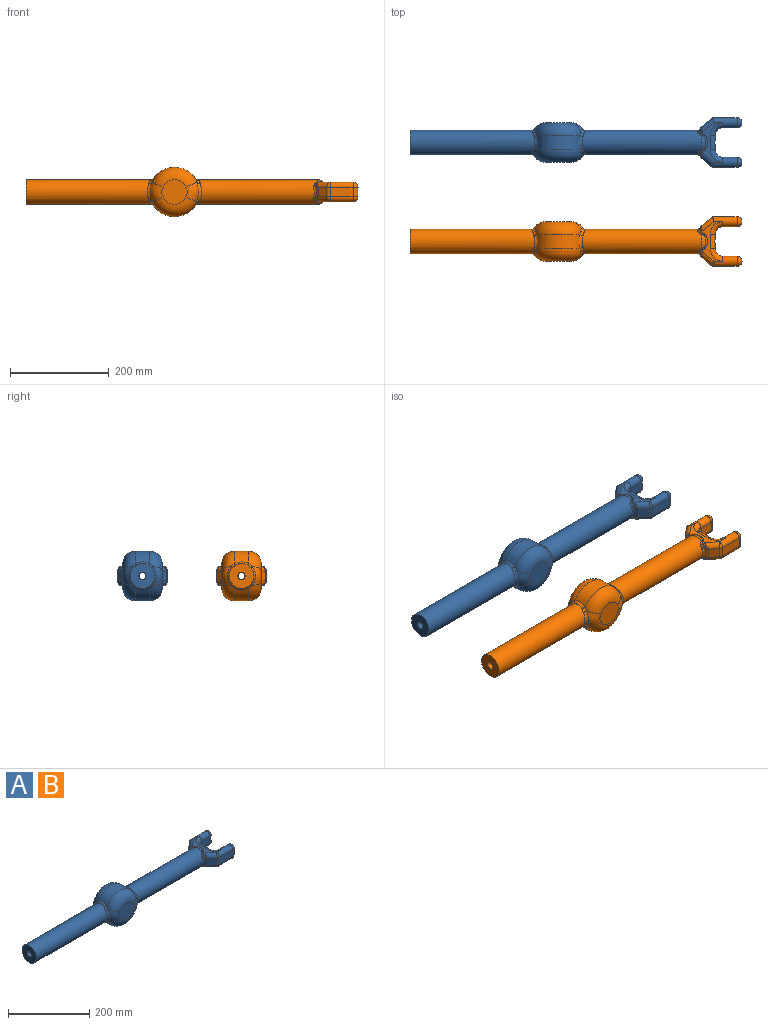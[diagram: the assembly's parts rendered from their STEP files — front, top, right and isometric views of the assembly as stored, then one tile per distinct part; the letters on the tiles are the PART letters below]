
ASSEMBLY  parts=2 mates=1
PART A: 117 faces, bbox 670.9x100x108.2 mm
  f0: cylinder r=50mm len=15mm, axis (0,1,0), area 22.9mm2, adj f10,f104
  f1: plane 20x4.5mm, normal (1,0,0), area 35mm2, adj f3,f4,f46,f114
  f2: plane 20x4.5mm, normal (1,0,0), area 35mm2, adj f3,f4,f45,f115
  f3: cylinder r=10mm len=30mm, axis (0,1,0), area 386.2mm2, adj f1,f2,f43,f52,f59,f116
  f4: cylinder r=10mm len=30mm, axis (0,-1,0), area 386.2mm2, adj f1,f2,f44,f65,f69,f113
  f5: cylinder r=50mm len=86.21mm, axis (0,1,0), area 2969.4mm2, adj f14,f19,f24,f33
  f6: cylinder r=25mm len=242.3mm, axis (-1,0,0), area 36737.8mm2, adj f21,f22,f23,f24,f25,f26,f27,f28
  f7: plane 54.17x50mm, normal (0,1,0), area 2000.6mm2, adj f17,f18,f19,f20
  f8: plane 54.17x50mm, normal (0,-1,0), area 2000.6mm2, adj f13,f14,f15,f16
  f9: cylinder r=50mm len=86.21mm, axis (0,1,0), area 2969.4mm2, adj f15,f18,f25,f32
  f10: cylinder r=7.5mm len=250.57mm, axis (-1,0,0), area 11807.6mm2, adj f0,f11
  f11: plane 50x50mm, normal (-1,0,0), area 1786.8mm2, adj f10,f12
  f12: cylinder r=25mm len=250mm, axis (-1,0,0), area 39081.8mm2, adj f11,f29,f30,f31,f32,f33,f34,f35
  f13: bspline ~42.42x28.46mm, area 843.8mm2, adj f8,f14,f15,f21
  f14: torus R=25mm, axis (0,-1,0), area 3684.3mm2, adj f5,f8,f13,f16,f22,f31
  f15: torus R=25mm, axis (0,-1,0), area 3684.3mm2, adj f8,f9,f13,f16,f23,f30
  f16: bspline ~42.42x28.46mm, area 843.8mm2, adj f8,f14,f15,f29
  f17: bspline ~41.4x27.73mm, area 843.8mm2, adj f7,f18,f19,f36
  f18: torus R=25mm, axis (0,-1,0), area 3684.3mm2, adj f7,f9,f17,f20,f27,f34
  f19: torus R=25mm, axis (0,-1,0), area 3684.3mm2, adj f5,f7,f17,f20,f26,f35
  f20: bspline ~41.4x27.73mm, area 843.8mm2, adj f7,f18,f19,f28
  f21: bspline ~40.1x10.75mm, area 316.1mm2, adj f6,f13,f22,f23
  f22: bspline ~14.61x11.73mm, area 76.1mm2, adj f6,f14,f21,f24
  f23: bspline ~14.61x11.73mm, area 76.1mm2, adj f6,f15,f21,f25
  f24: bspline ~36.68x9.98mm, area 221.1mm2, adj f5,f6,f22,f26
  f25: bspline ~36.68x9.98mm, area 221.1mm2, adj f6,f9,f23,f27
  f26: bspline ~13.29x10.22mm, area 76.1mm2, adj f6,f19,f24,f28
  f27: bspline ~14.61x11.73mm, area 76.1mm2, adj f6,f18,f25,f28
  f28: bspline ~40.1x10.75mm, area 316.1mm2, adj f6,f20,f26,f27
  f29: bspline ~40.1x10.75mm, area 316.1mm2, adj f12,f16,f30,f31
  f30: bspline ~14.61x11.73mm, area 76.1mm2, adj f12,f15,f29,f32
  f31: bspline ~14.61x11.73mm, area 76.1mm2, adj f12,f14,f29,f33
  f32: bspline ~36.68x9.98mm, area 221.1mm2, adj f9,f12,f30,f34
  f33: bspline ~36.68x9.98mm, area 221.1mm2, adj f5,f12,f31,f35
  f34: bspline ~14.61x11.73mm, area 76.1mm2, adj f12,f18,f32,f36
  f35: bspline ~14.61x11.73mm, area 76.1mm2, adj f12,f19,f33,f36
  f36: bspline ~40.1x10.75mm, area 316.1mm2, adj f12,f17,f34,f35
  f37: plane 20.82x20mm, normal (-0.63,0.77,0), area 537.5mm2, adj f38,f61,f63,f66
  f38: plane 50x20mm, normal (0,1,0), area 1000mm2, adj f37,f58,f64,f68
  f39: plane 28.61x20mm, normal (0,-1,0), area 572.2mm2, adj f46,f58,f64,f68
  f40: plane 28.61x20mm, normal (0,1,0), area 572.2mm2, adj f45,f47,f53,f60
  f41: plane 46.44x20mm, normal (0,-1,0), area 928.7mm2, adj f47,f53,f54,f60
  f42: plane 20x18.06mm, normal (-0.63,-0.77,0), area 466.2mm2, adj f48,f51,f54,f55
  f43: plane 80x40.89mm, normal (0,0,-1), area 856.7mm2, adj f3,f47,f48,f52,f58,f59,f61,f74
  f44: plane 80x40.89mm, normal (0,0,1), area 856.7mm2, adj f4,f55,f60,f65,f66,f68,f69,f77
  f45: cylinder r=15mm len=20mm, axis (0,0,1), area 471.2mm2, adj f2,f40,f52,f65
  f46: cylinder r=15mm len=20mm, axis (0,0,1), area 471.2mm2, adj f1,f39,f59,f69
  f47: cylinder r=10mm len=46.44mm, axis (1,0,0), area 1178.8mm2, adj f40,f41,f43,f49,f50,f52
  f48: cylinder r=10mm len=29.38mm, axis (0.77,-0.63,0), area 418.7mm2, adj f42,f43,f50,f72,f73
  f49: sphere r=10mm, area 257.1mm2, adj f47,f53
  f50: sphere r=10mm, area 43.6mm2, adj f47,f48,f54
  f51: cylinder r=10mm len=27.07mm, axis (0,0,-1), area 144.6mm2, adj f42,f72,f75,f85
  f52: torus R=25mm, axis (0,0,1), area 459.8mm2, adj f3,f43,f45,f47
  f53: cylinder r=10mm len=20mm, axis (0,0,-1), area 628.3mm2, adj f40,f41,f49,f56
  f54: cylinder r=10mm len=20mm, axis (0,0,-1), area 137mm2, adj f41,f42,f50,f57
  f55: cylinder r=10mm len=29.38mm, axis (-0.77,0.63,0), area 418.7mm2, adj f42,f44,f57,f75,f76
  f56: sphere r=10mm, area 314.2mm2, adj f53,f60
  f57: sphere r=10mm, area 68.5mm2, adj f54,f55,f60
  f58: cylinder r=10mm len=50mm, axis (-1,0,0), area 1206.8mm2, adj f38,f39,f43,f59,f61,f62
  f59: torus R=25mm, axis (0,0,1), area 459.8mm2, adj f3,f43,f46,f58
  f60: cylinder r=10mm len=46.44mm, axis (-1,0,0), area 1178.8mm2, adj f40,f41,f44,f56,f57,f65
  f61: cylinder r=10mm len=32.14mm, axis (-0.77,-0.63,0), area 446.7mm2, adj f37,f43,f58,f78,f79
  f62: sphere r=10mm, area 257.1mm2, adj f58,f64
  f63: cylinder r=10mm len=27.07mm, axis (0,0,-1), area 144.6mm2, adj f37,f78,f81,f102
  f64: cylinder r=10mm len=20mm, axis (0,0,-1), area 628.3mm2, adj f38,f39,f62,f67
  f65: torus R=25mm, axis (0,0,1), area 459.8mm2, adj f4,f44,f45,f60
  f66: cylinder r=10mm len=32.14mm, axis (0.77,0.63,0), area 446.7mm2, adj f37,f44,f68,f81,f82
  f67: sphere r=10mm, area 314.2mm2, adj f64,f68
  f68: cylinder r=10mm len=50mm, axis (1,0,0), area 1206.8mm2, adj f38,f39,f44,f66,f67,f69
  f69: torus R=25mm, axis (0,0,1), area 459.8mm2, adj f4,f44,f46,f68
  f70: torus R=15mm, axis (1,0,0), area 189mm2, adj f6,f90,f92,f94
  f71: torus R=15mm, axis (1,0,0), area 189mm2, adj f6,f93,f95,f97
  f72: bspline ~9.03x8.5mm, area 28mm2, adj f48,f51,f73,f84
  f73: bspline ~6.53x5.56mm, area 30.8mm2, adj f48,f72,f74,f86
  f74: cylinder r=5mm len=4.71mm, axis (0,-1,0), area 13mm2, adj f43,f73,f88,f90
  f75: bspline ~9.03x8.5mm, area 28mm2, adj f51,f55,f76,f87
  f76: bspline ~9.61x7.08mm, area 30.8mm2, adj f55,f75,f77,f89
  f77: cylinder r=5mm len=4.71mm, axis (0,1,0), area 13mm2, adj f44,f76,f91,f93
  f78: bspline ~9.03x8.5mm, area 28mm2, adj f61,f63,f79,f100
  f79: bspline ~9.61x7.08mm, area 30.8mm2, adj f61,f78,f80,f98
  f80: cylinder r=5mm len=4.71mm, axis (0,-1,0), area 13mm2, adj f43,f79,f94,f96
  f81: bspline ~9.03x8.5mm, area 28mm2, adj f63,f66,f82,f103
  f82: bspline ~6.53x5.56mm, area 30.8mm2, adj f66,f81,f83,f101
  f83: cylinder r=5mm len=4.71mm, axis (0,1,0), area 13mm2, adj f44,f82,f97,f99
  f84: bspline ~5.26x5.04mm, area 8.5mm2, adj f6,f72,f85,f86
  f85: bspline ~30.41x7.05mm, area 165.9mm2, adj f6,f51,f84,f87
  f86: bspline ~9.05x6.73mm, area 39mm2, adj f6,f73,f84,f88
  f87: bspline ~5.78x5.11mm, area 8.5mm2, adj f6,f75,f85,f89
  f88: bspline ~8.58x8.41mm, area 28.3mm2, adj f6,f74,f86,f90
  f89: bspline ~9.05x6.73mm, area 39mm2, adj f6,f76,f87,f91
  f90: bspline ~3.95x3.78mm, area 2.5mm2, adj f70,f74,f88,f92
  f91: bspline ~8.58x8.41mm, area 28.3mm2, adj f6,f77,f89,f93
  f92: bspline ~33.18x11.88mm, area 134.7mm2, adj f43,f70,f90,f94
  f93: bspline ~3.95x3.78mm, area 2.5mm2, adj f71,f77,f91,f95
  f94: bspline ~3.95x3.78mm, area 2.5mm2, adj f70,f80,f92,f96
  f95: bspline ~33.18x11.88mm, area 134.7mm2, adj f44,f71,f93,f97
  f96: bspline ~8.58x8.41mm, area 28.3mm2, adj f6,f80,f94,f98
  f97: bspline ~3.95x3.78mm, area 2.5mm2, adj f71,f83,f95,f99
  f98: bspline ~9.05x6.73mm, area 39mm2, adj f6,f79,f96,f100
  f99: bspline ~8.58x8.41mm, area 28.3mm2, adj f6,f83,f97,f101
  f100: bspline ~5.78x5.11mm, area 8.5mm2, adj f6,f78,f98,f102
  f101: bspline ~9.05x6.73mm, area 39mm2, adj f6,f82,f99,f103
  f102: bspline ~30.41x7.05mm, area 165.9mm2, adj f6,f63,f100,f103
  f103: bspline ~5.26x5.04mm, area 8.5mm2, adj f6,f81,f101,f102
  f104: cylinder r=7mm len=99.02mm, axis (1,0,0), area 4354.9mm2, adj f0,f108
  f105: cylinder r=7mm len=19.57mm, axis (1,0,0), area 860.5mm2, adj f109,f112
  f106: plane 21x21mm, normal (1,0,0), area 145.3mm2, adj f111,f112
  f107: cylinder r=12.5mm len=25mm, axis (1,0,0), area 482.2mm2, adj f111,f113,f114,f115,f116
  f108: cylinder r=50mm len=15mm, axis (0,1,0), area 22.9mm2, adj f104,f110
  f109: plane 15x15mm, normal (-1,0,0), area 22.8mm2, adj f105,f110
  f110: cylinder r=7.5mm len=236.99mm, axis (-1,0,0), area 11167.9mm2, adj f108,f109
  f111: cone r=10.5mm half-angle=45deg, axis (1,0,0), area 204.4mm2, adj f106,f107
  f112: cone r=7mm half-angle=45deg, axis (1,0,0), area 66.6mm2, adj f105,f106
  f113: bspline ~23.54x8.54mm, area 85mm2, adj f4,f107,f114,f115
  f114: torus R=14.5mm, axis (1,0,0), area 63.2mm2, adj f1,f107,f113,f116
  f115: torus R=14.5mm, axis (1,0,0), area 63.2mm2, adj f2,f107,f113,f116
  f116: bspline ~23.54x8.54mm, area 85mm2, adj f3,f107,f114,f115
PART B: same geometry as A
PLACE A rot(axis=(0.7,0.71,0.06),0deg) t=(-155.16,-85.99,-25.32)mm
PLACE B rot(axis=(0.7,0.71,0.06),0deg) t=(-155.16,-285.99,-25.32)mm
MATE revolute B.f0 <-> A.f0  axis (0,-1,0) through (-155.16,-325.99,-25.32)mm
